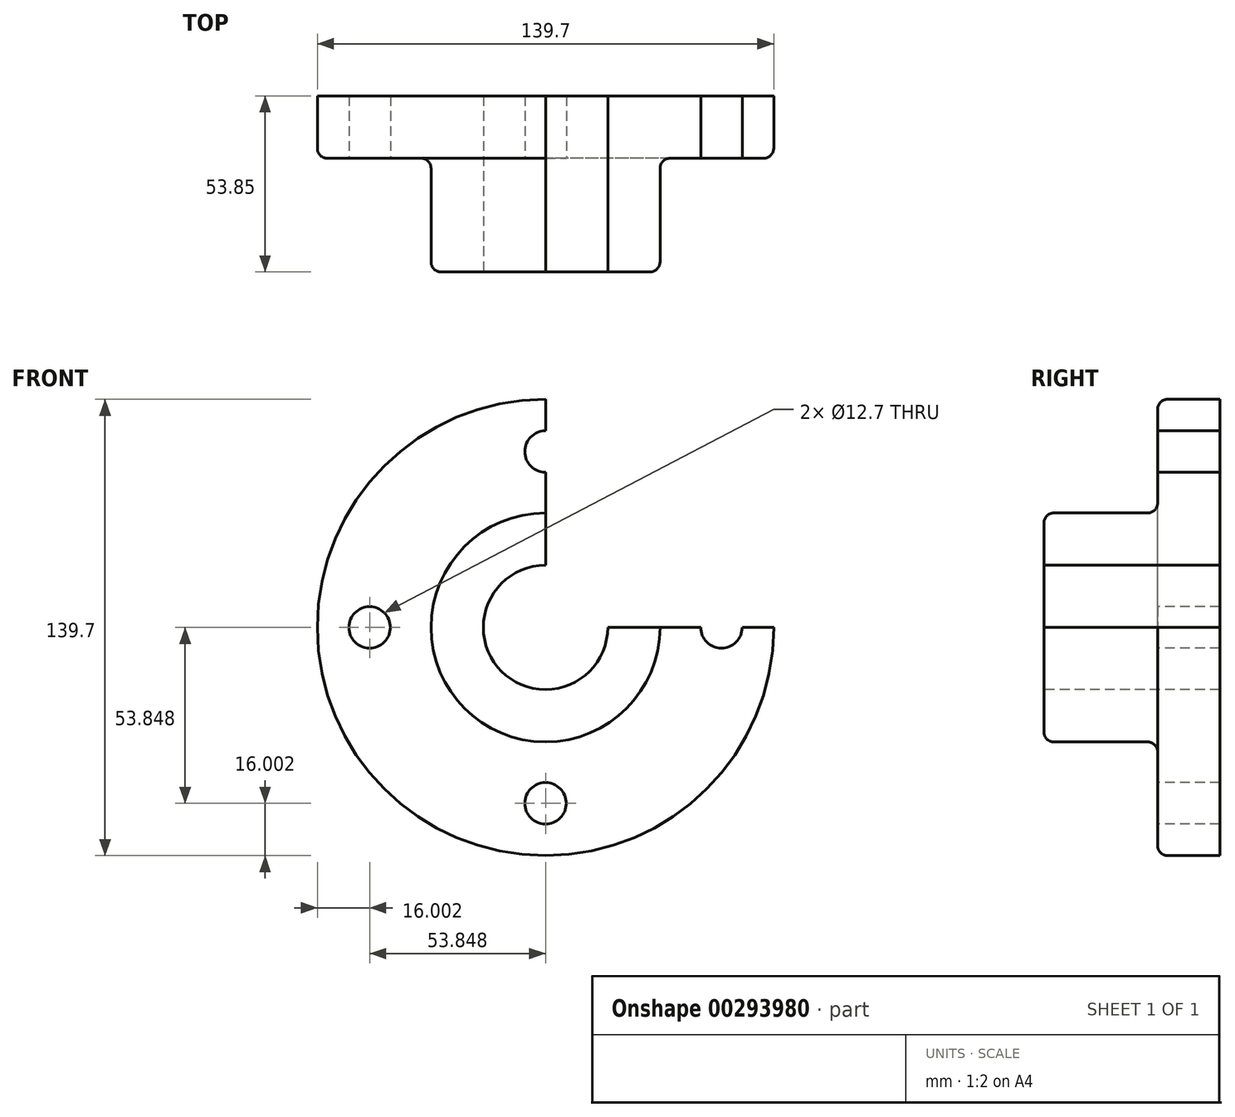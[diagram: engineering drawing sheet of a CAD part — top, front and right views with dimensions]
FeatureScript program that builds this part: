
annotation { "Feature Type Name" : "Feature", "Feature Type Description" : "" }
export const myFeature = defineFeature(function(context is Context, id is Id, definition is map)
    precondition{}
    {
        {
            var Q0;
            Q0=qCreatedBy(makeId("Top.planeOp"),FACE);
            var sketch = newSketch(context, id + "F0", { "sketchPlane" : qUnion([Q0])});
            skLineSegment(sketch, "E0", {"start": v(19.05, 0) * mm, "end": v(19.05, 53.85) * mm});
            skLineSegment(sketch, "E1", {"start": v(69.85, 53.85) * mm, "end": v(69.85, 34.8) * mm});
            skLineSegment(sketch, "E2", {"start": v(69.85, 34.8) * mm, "end": v(35.05, 34.8) * mm});
            skLineSegment(sketch, "E3", {"start": v(35.05, 34.8) * mm, "end": v(35.05, 0) * mm});
            skLineSegment(sketch, "E4", {"start": v(35.05, 0) * mm, "end": v(19.05, 0) * mm});
            skLineSegment(sketch, "E5", {"start": v(19.05, 53.85) * mm, "end": v(69.85, 53.85) * mm});
            skLineSegment(sketch, "E6", {"start": v(0, 0) * mm, "end": v(0, 68.9) * mm, "construction": true});
            skSolve(sketch);
        }
        {
            var Q0;
            Q0=makeQuery(id+"F0.imprint","IMPRINT",FACE,{"disambiguationData":[TD([[makeQuery(id+"F0.imprint","IMPRINT",EDGE,{"derivedFrom":sQuery(id+"F0.wireOp",EDGE,"E0")}),-1.0]])]});
            var Q1;
            Q1=sQuery(id+"F0.wireOp",EDGE,"E6");
            revolve(context, id + "F1", {"entities" : qUnion([Q0]), "axis" : qUnion([Q1]), "revolveType" : RevolveType.ONE_DIRECTION, "angle" : 270 * degree});
        }
        {
            var Q0;
            Q0=qCreatedBy(makeId("Front.planeOp"),FACE);
            var sketch = newSketch(context, id + "F2", { "sketchPlane" : qUnion([Q0])});
            skCircle(sketch, "E7", {"center": v(0, 0) * mm, "radius": 53.85 * mm, "construction": true});
            skCircle(sketch, "E8", {"center": v(0, 53.85) * mm, "radius": 6.35 * mm});
            skCircle(sketch, "E9", {"center": v(-53.85, 0) * mm, "radius": 6.35 * mm});
            skCircle(sketch, "E10", {"center": v(53.85, 0) * mm, "radius": 6.35 * mm});
            skCircle(sketch, "E11", {"center": v(0, -53.85) * mm, "radius": 6.35 * mm});
            skSolve(sketch);
        }
        {
            var Q0;
            Q0=makeQuery(id+"F1.opRevolve","SWEPT_EDGE",EDGE,{"disambiguationData":[OSD([sQuery(id+"F0.wireOp",EDGE,"E1"),sQuery(id+"F0.wireOp",EDGE,"E2")])]});
            var Q1;
            Q1=makeQuery(id+"F1.opRevolve","SWEPT_EDGE",EDGE,{"disambiguationData":[OSD([sQuery(id+"F0.wireOp",EDGE,"E3"),sQuery(id+"F0.wireOp",EDGE,"E4")])]});
            var Q2;
            Q2=makeQuery(id+"F1.opRevolve","SWEPT_EDGE",EDGE,{"disambiguationData":[OSD([sQuery(id+"F0.wireOp",EDGE,"E2"),sQuery(id+"F0.wireOp",EDGE,"E3")])]});
            fillet(context, id + "F3", {"entities" : qUnion([Q0, Q1, Q2]), "radius" : 3.05 * mm, "tangentPropagation" : true, "allowEdgeOverflow" : false});
        }
        {
            var Q0;
            Q0=makeQuery(id+"F2.imprint","IMPRINT",FACE,{"disambiguationData":[TD([[makeQuery(id+"F2.imprint","IMPRINT",EDGE,{"derivedFrom":sQuery(id+"F2.wireOp",EDGE,"E8")}),1.0]])]});
            var Q1;
            Q1=makeQuery(id+"F2.imprint","IMPRINT",FACE,{"disambiguationData":[TD([[makeQuery(id+"F2.imprint","IMPRINT",EDGE,{"derivedFrom":sQuery(id+"F2.wireOp",EDGE,"E10")}),1.0]])]});
            var Q2;
            Q2=makeQuery(id+"F2.imprint","IMPRINT",FACE,{"disambiguationData":[TD([[makeQuery(id+"F2.imprint","IMPRINT",EDGE,{"derivedFrom":sQuery(id+"F2.wireOp",EDGE,"E11")}),1.0]])]});
            var Q3;
            Q3=makeQuery(id+"F2.imprint","IMPRINT",FACE,{"disambiguationData":[TD([[makeQuery(id+"F2.imprint","IMPRINT",EDGE,{"derivedFrom":sQuery(id+"F2.wireOp",EDGE,"E9")}),1.0]])]});
            extrude(context, id + "F4", {"entities" : qUnion([Q0, Q1, Q2, Q3]), "operationType" : NewBodyOperationType.REMOVE, "endBound" : BoundingType.THROUGH_ALL, "oppositeDirection" : true, "depth" : 25.4 * mm});
        }
    });
